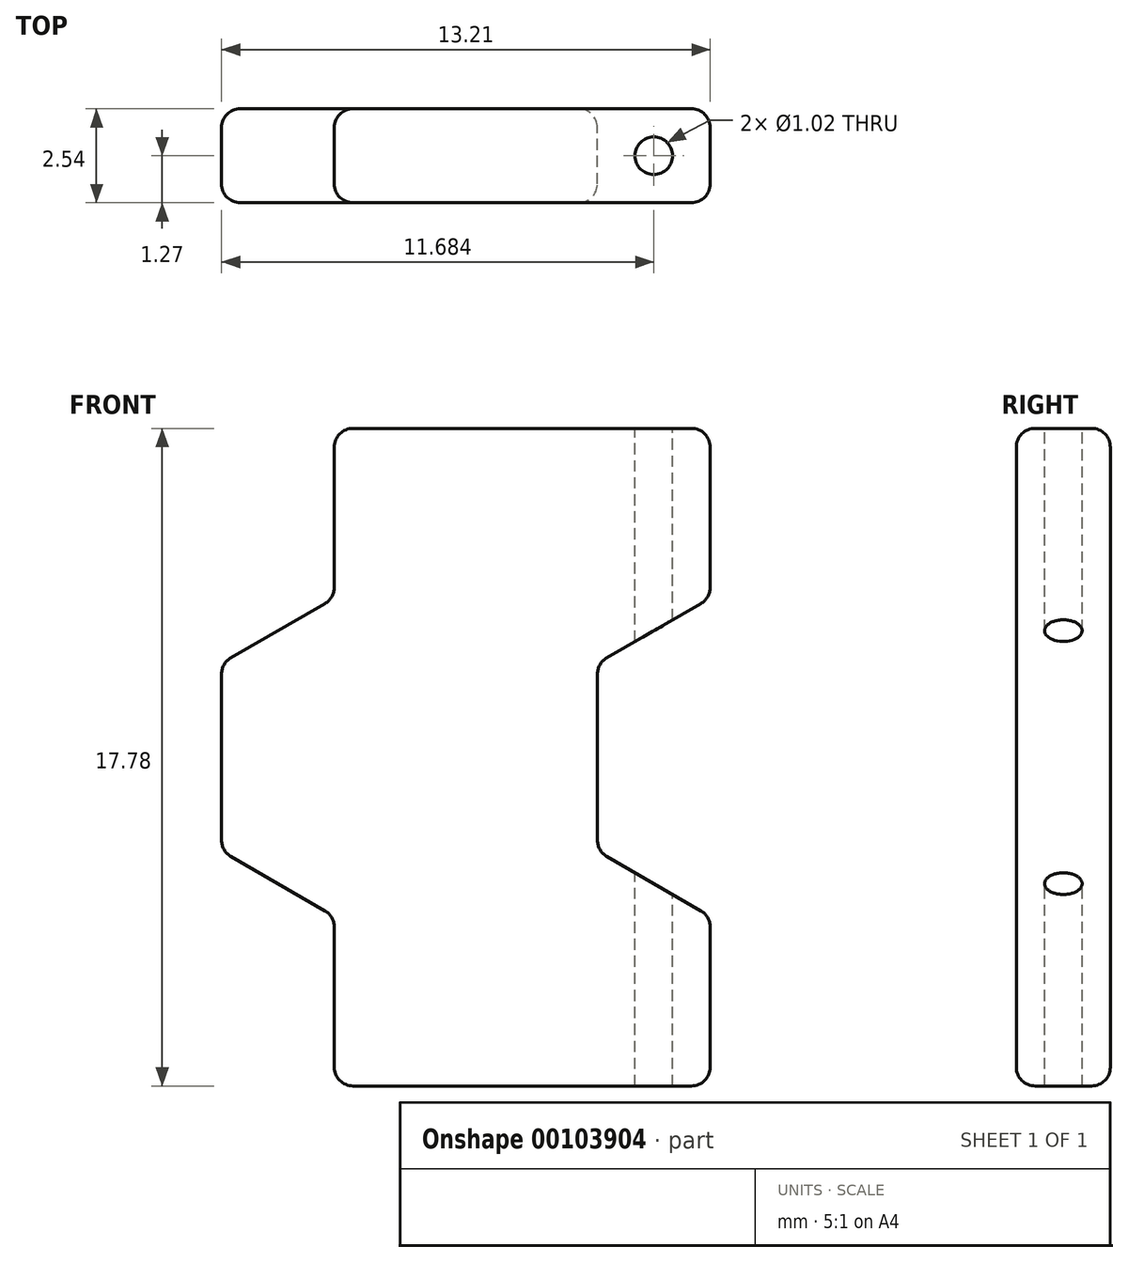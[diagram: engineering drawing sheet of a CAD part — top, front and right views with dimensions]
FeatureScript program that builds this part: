
annotation { "Feature Type Name" : "Feature", "Feature Type Description" : "" }
export const myFeature = defineFeature(function(context is Context, id is Id, definition is map)
    precondition{}
    {
        {
            var Q0;
            Q0=qCreatedBy(makeId("Front.planeOp"),FACE);
            var sketch = newSketch(context, id + "F0", { "sketchPlane" : qUnion([Q0])});
            skLineSegment(sketch, "E0", {"start": v(-10.16, 0) * mm, "end": v(-10.16, 2.54) * mm});
            skLineSegment(sketch, "E1", {"start": v(-10.16, 2.54) * mm, "end": v(-7.11, 4.3) * mm});
            skLineSegment(sketch, "E2", {"start": v(-7.11, 4.3) * mm, "end": v(-7.11, 8.9) * mm});
            skLineSegment(sketch, "E3", {"start": v(-7.11, 8.9) * mm, "end": v(3.05, 8.9) * mm});
            skLineSegment(sketch, "E4", {"start": v(3.05, 8.9) * mm, "end": v(3.05, 4.3) * mm});
            skLineSegment(sketch, "E5", {"start": v(3.05, 4.3) * mm, "end": v(0, 2.54) * mm});
            skLineSegment(sketch, "E6", {"start": v(0, 2.54) * mm, "end": v(0, 0) * mm});
            skLineSegment(sketch, "E7.MirrorCS", {"start": v(-10.16, 0) * mm, "end": v(-10.16, -2.54) * mm});
            skLineSegment(sketch, "E8.MirrorCS", {"start": v(-10.16, -2.54) * mm, "end": v(-7.11, -4.3) * mm});
            skLineSegment(sketch, "E9.MirrorCS", {"start": v(-7.11, -4.3) * mm, "end": v(-7.11, -8.9) * mm});
            skLineSegment(sketch, "E10.MirrorCS", {"start": v(-7.11, -8.9) * mm, "end": v(3.05, -8.9) * mm});
            skLineSegment(sketch, "E11.MirrorCS", {"start": v(3.05, -8.9) * mm, "end": v(3.05, -4.3) * mm});
            skLineSegment(sketch, "E12.MirrorCS", {"start": v(0, -2.54) * mm, "end": v(0, 0) * mm});
            skLineSegment(sketch, "E13.MirrorCS", {"start": v(3.05, -4.3) * mm, "end": v(0, -2.54) * mm});
            skSolve(sketch);
        }
        {
            var Q0;
            Q0 = qSketchRegion(id + "F0", true);
            extrude(context, id + "F1", {"entities" : qUnion([Q0]), "depth" : 2.54 * mm});
        }
        {
            var Q0;
            Q0=makeQuery(id+"F1.opExtrude","SWEPT_FACE",FACE,{"disambiguationData":[OSD([sQuery(id+"F0.wireOp",EDGE,"E3")])]});
            var sketch = newSketch(context, id + "F2", { "sketchPlane" : qUnion([Q0])});
            skCircle(sketch, "E14", {"center": v(1.52, -1.27) * mm, "radius": 0.5 * mm});
            skPoint(sketch, "E14.centerSnap0", {"position": v(3.05, -1.27) * mm});
            skLineSegment(sketch, "E15", {"start": v(-3.6, -2.54) * mm, "end": v(-3.6, 0) * mm, "construction": true});
            skCircle(sketch, "E16.MirrorC", {"center": v(-8.74, -1.27) * mm, "radius": 0.5 * mm});
            skSolve(sketch);
        }
        {
            var Q0;
            Q0=makeQuery(id+"F2.imprint","IMPRINT",FACE,{"disambiguationData":[TD([[makeQuery(id+"F2.imprint","IMPRINT",EDGE,{"derivedFrom":sQuery(id+"F2.wireOp",EDGE,"E14")}),1.0]])]});
            var Q1;
            Q1=makeQuery(id+"F2.imprint","IMPRINT",FACE,{"disambiguationData":[TD([[makeQuery(id+"F2.imprint","IMPRINT",EDGE,{"derivedFrom":sQuery(id+"F2.wireOp",EDGE,"E16.MirrorC")}),-1.0]])]});
            extrude(context, id + "F3", {"entities" : qUnion([Q0, Q1]), "operationType" : NewBodyOperationType.REMOVE, "oppositeDirection" : true, "depth" : 25.4 * mm});
        }
        {
            var Q0;
            Q0=makeQuery(id+"F1.opExtrude","CAP_FACE",FACE,{"disambiguationData":[OSD([sQuery(id+"F0.wireOp",EDGE,"E0"),sQuery(id+"F0.wireOp",EDGE,"E1"),sQuery(id+"F0.wireOp",EDGE,"E2"),sQuery(id+"F0.wireOp",EDGE,"E3"),sQuery(id+"F0.wireOp",EDGE,"E4"),sQuery(id+"F0.wireOp",EDGE,"E5"),sQuery(id+"F0.wireOp",EDGE,"E6"),sQuery(id+"F0.wireOp",EDGE,"E7.MirrorCS"),sQuery(id+"F0.wireOp",EDGE,"E8.MirrorCS"),sQuery(id+"F0.wireOp",EDGE,"E9.MirrorCS"),sQuery(id+"F0.wireOp",EDGE,"E10.MirrorCS"),sQuery(id+"F0.wireOp",EDGE,"E11.MirrorCS"),sQuery(id+"F0.wireOp",EDGE,"E12.MirrorCS"),sQuery(id+"F0.wireOp",EDGE,"E13.MirrorCS")])],"isStart":true});
            var Q1;
            Q1=makeQuery(id+"F1.opExtrude","CAP_FACE",FACE,{"disambiguationData":[OSD([sQuery(id+"F0.wireOp",EDGE,"E0"),sQuery(id+"F0.wireOp",EDGE,"E1"),sQuery(id+"F0.wireOp",EDGE,"E2"),sQuery(id+"F0.wireOp",EDGE,"E3"),sQuery(id+"F0.wireOp",EDGE,"E4"),sQuery(id+"F0.wireOp",EDGE,"E5"),sQuery(id+"F0.wireOp",EDGE,"E6"),sQuery(id+"F0.wireOp",EDGE,"E7.MirrorCS"),sQuery(id+"F0.wireOp",EDGE,"E8.MirrorCS"),sQuery(id+"F0.wireOp",EDGE,"E9.MirrorCS"),sQuery(id+"F0.wireOp",EDGE,"E10.MirrorCS"),sQuery(id+"F0.wireOp",EDGE,"E11.MirrorCS"),sQuery(id+"F0.wireOp",EDGE,"E12.MirrorCS"),sQuery(id+"F0.wireOp",EDGE,"E13.MirrorCS")])],"isStart":false});
            var Q2;
            Q2=makeQuery(id+"F1.opExtrude","SWEPT_EDGE",EDGE,{"disambiguationData":[OSD([sQuery(id+"F0.wireOp",EDGE,"E10.MirrorCS"),sQuery(id+"F0.wireOp",EDGE,"E11.MirrorCS")])]});
            var Q3;
            Q3=makeQuery(id+"F1.opExtrude","SWEPT_EDGE",EDGE,{"disambiguationData":[OSD([sQuery(id+"F0.wireOp",EDGE,"E2"),sQuery(id+"F0.wireOp",EDGE,"E3")])]});
            var Q4;
            Q4=makeQuery(id+"F1.opExtrude","SWEPT_EDGE",EDGE,{"disambiguationData":[OSD([sQuery(id+"F0.wireOp",EDGE,"E1"),sQuery(id+"F0.wireOp",EDGE,"E2")])]});
            var Q5;
            Q5=makeQuery(id+"F1.opExtrude","SWEPT_EDGE",EDGE,{"disambiguationData":[OSD([sQuery(id+"F0.wireOp",EDGE,"E0"),sQuery(id+"F0.wireOp",EDGE,"E1")])]});
            var Q6;
            Q6=makeQuery(id+"F1.opExtrude","SWEPT_EDGE",EDGE,{"disambiguationData":[OSD([sQuery(id+"F0.wireOp",EDGE,"E3"),sQuery(id+"F0.wireOp",EDGE,"E4")])]});
            var Q7;
            Q7=makeQuery(id+"F1.opExtrude","SWEPT_EDGE",EDGE,{"disambiguationData":[OSD([sQuery(id+"F0.wireOp",EDGE,"E11.MirrorCS"),sQuery(id+"F0.wireOp",EDGE,"E13.MirrorCS")])]});
            var Q8;
            Q8=makeQuery(id+"F1.opExtrude","SWEPT_EDGE",EDGE,{"disambiguationData":[OSD([sQuery(id+"F0.wireOp",EDGE,"E4"),sQuery(id+"F0.wireOp",EDGE,"E5")])]});
            var Q9;
            Q9=makeQuery(id+"F1.opExtrude","SWEPT_EDGE",EDGE,{"disambiguationData":[OSD([sQuery(id+"F0.wireOp",EDGE,"E5"),sQuery(id+"F0.wireOp",EDGE,"E6")])]});
            var Q10;
            Q10=makeQuery(id+"F1.opExtrude","SWEPT_EDGE",EDGE,{"disambiguationData":[OSD([sQuery(id+"F0.wireOp",EDGE,"E12.MirrorCS"),sQuery(id+"F0.wireOp",EDGE,"E13.MirrorCS")])]});
            var Q11;
            Q11=makeQuery(id+"F1.opExtrude","SWEPT_EDGE",EDGE,{"disambiguationData":[OSD([sQuery(id+"F0.wireOp",EDGE,"E9.MirrorCS"),sQuery(id+"F0.wireOp",EDGE,"E10.MirrorCS")])]});
            var Q12;
            Q12=makeQuery(id+"F1.opExtrude","SWEPT_EDGE",EDGE,{"disambiguationData":[OSD([sQuery(id+"F0.wireOp",EDGE,"E8.MirrorCS"),sQuery(id+"F0.wireOp",EDGE,"E9.MirrorCS")])]});
            var Q13;
            Q13=makeQuery(id+"F1.opExtrude","SWEPT_EDGE",EDGE,{"disambiguationData":[OSD([sQuery(id+"F0.wireOp",EDGE,"E7.MirrorCS"),sQuery(id+"F0.wireOp",EDGE,"E8.MirrorCS")])]});
            fillet(context, id + "F4", {"entities" : qUnion([Q0, Q1, Q2, Q3, Q4, Q5, Q6, Q7, Q8, Q9, Q10, Q11, Q12, Q13]), "radius" : 0.5 * mm, "tangentPropagation" : true, "allowEdgeOverflow" : false});
        }
    });
